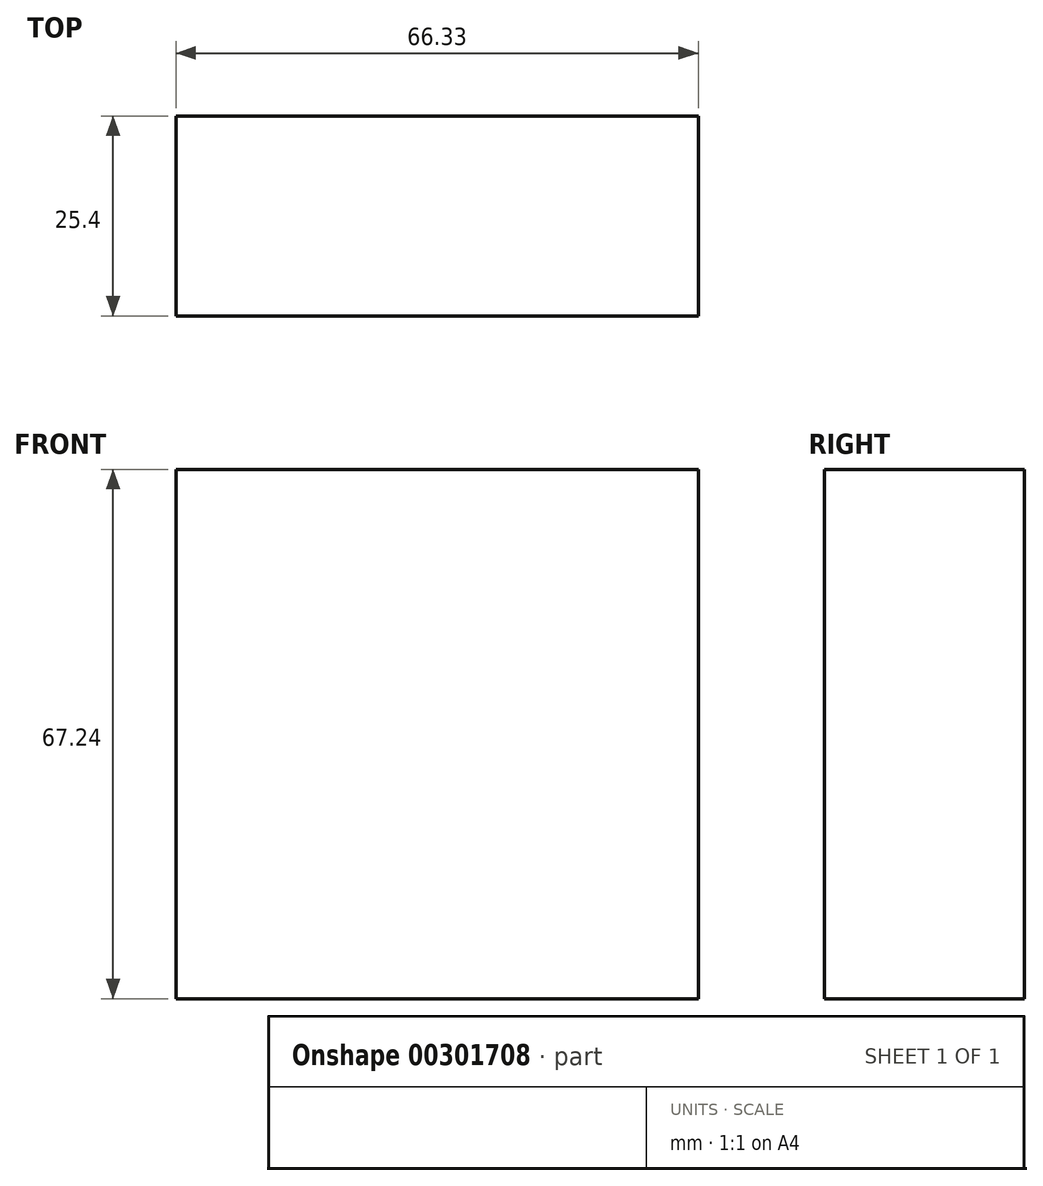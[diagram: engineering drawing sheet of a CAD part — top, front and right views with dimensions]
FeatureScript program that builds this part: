
annotation { "Feature Type Name" : "Feature", "Feature Type Description" : "" }
export const myFeature = defineFeature(function(context is Context, id is Id, definition is map)
    precondition{}
    {
        {
            var Q0;
            Q0=qCreatedBy(makeId("Front.planeOp"),FACE);
            var sketch = newSketch(context, id + "F0", { "sketchPlane" : qUnion([Q0])});
            skLineSegment(sketch, "E0.bottom", {"start": v(-105.47, -20.33) * mm, "end": v(-39.14, -20.33) * mm});
            skLineSegment(sketch, "E0.top", {"start": v(-105.47, 46.9) * mm, "end": v(-39.14, 46.9) * mm});
            skLineSegment(sketch, "E0.left", {"start": v(-105.47, -20.33) * mm, "end": v(-105.47, 46.9) * mm});
            skLineSegment(sketch, "E0.right", {"start": v(-39.14, -20.33) * mm, "end": v(-39.14, 46.9) * mm});
            skSolve(sketch);
        }
        {
            var Q0;
            Q0=makeQuery(id+"F0.imprint","IMPRINT",FACE,{"disambiguationData":[TD([[makeQuery(id+"F0.imprint","IMPRINT",EDGE,{"derivedFrom":sQuery(id+"F0.wireOp",EDGE,"E0.bottom")}),1.0]])]});
            extrude(context, id + "F1", {"entities" : qUnion([Q0]), "depth" : 25.4 * mm});
        }
    });
